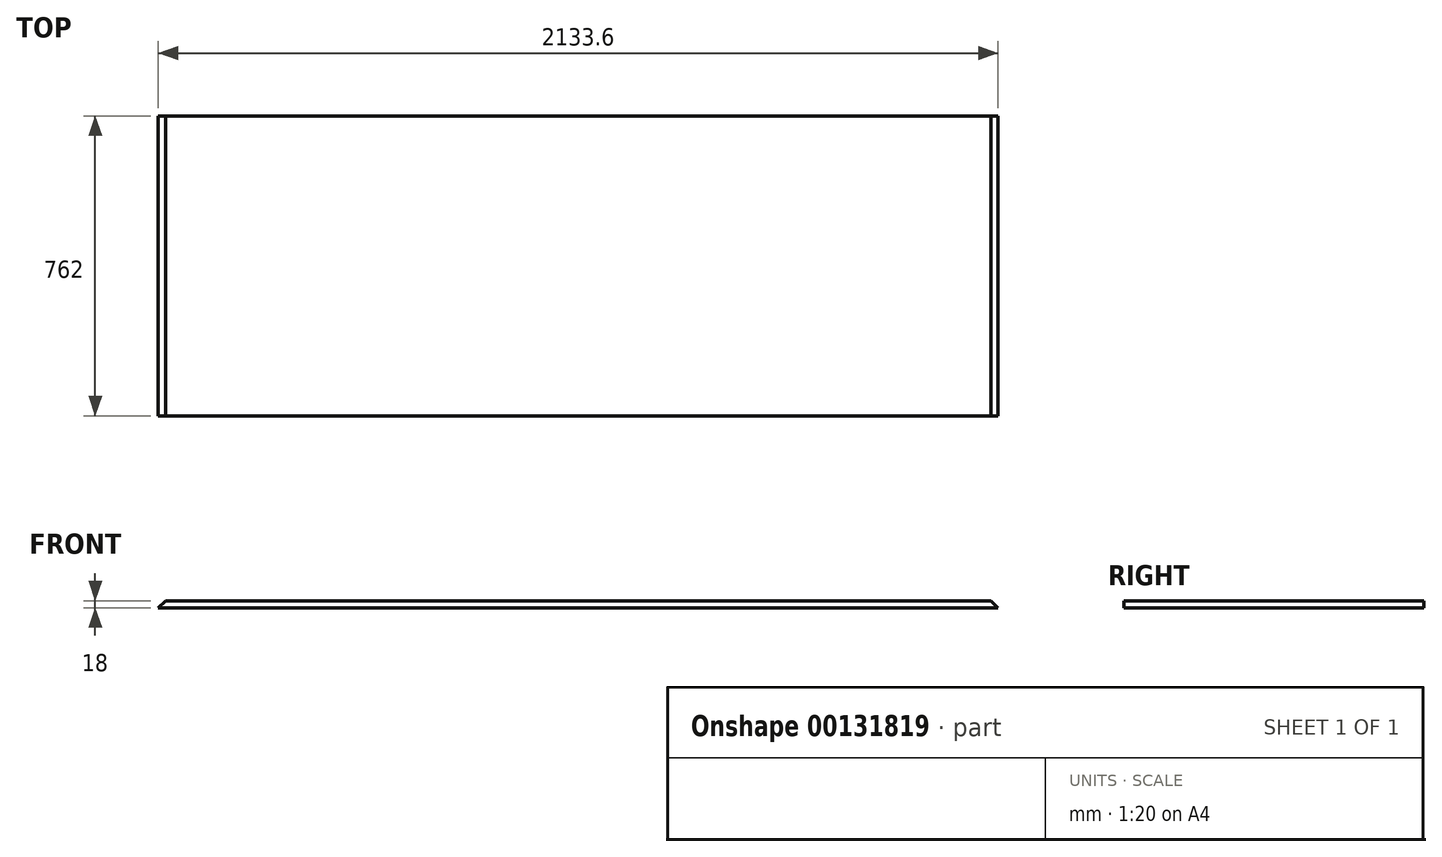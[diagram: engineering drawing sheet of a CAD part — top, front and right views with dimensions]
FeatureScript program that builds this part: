
annotation { "Feature Type Name" : "Feature", "Feature Type Description" : "" }
export const myFeature = defineFeature(function(context is Context, id is Id, definition is map)
    precondition{}
    {
        {
            var Q0;
            Q0=qCreatedBy(makeId("Top.planeOp"),FACE);
            var sketch = newSketch(context, id + "F0", { "sketchPlane" : qUnion([Q0])});
            skLineSegment(sketch, "E0.bottom", {"start": v(0, 0) * mm, "end": v(2133.6, 0) * mm});
            skLineSegment(sketch, "E0.top", {"start": v(0, 762) * mm, "end": v(2133.6, 762) * mm});
            skLineSegment(sketch, "E0.left", {"start": v(0, 0) * mm, "end": v(0, 762) * mm});
            skLineSegment(sketch, "E0.right", {"start": v(2133.6, 0) * mm, "end": v(2133.6, 762) * mm});
            skSolve(sketch);
        }
        {
            var Q0;
            Q0 = qSketchRegion(id + "F0", true);
            extrude(context, id + "F1", {"entities" : qUnion([Q0]), "depth" : 18 * mm});
        }
        {
            var Q0;
            Q0=makeQuery(id+"F1.opExtrude","CAP_EDGE",EDGE,{"disambiguationData":[OSD([sQuery(id+"F0.wireOp",EDGE,"E0.right")])],"isStart":false});
            var Q1;
            Q1=makeQuery(id+"F1.opExtrude","CAP_EDGE",EDGE,{"disambiguationData":[OSD([sQuery(id+"F0.wireOp",EDGE,"E0.left")])],"isStart":false});
            chamfer(context, id + "F2", {"entities" : qUnion([Q0, Q1]), "width" : 18 * mm, "tangentPropagation" : true});
        }
    });
